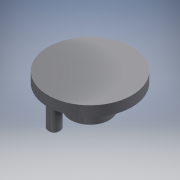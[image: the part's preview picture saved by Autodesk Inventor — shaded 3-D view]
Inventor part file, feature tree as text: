
AUTODESK INVENTOR PART (.ipt)
format: ipt  version: 2016 (Build 200138000, 138)  size: 146,944 bytes
history: native  units: mm
features: plane x4, extrude x4, sketch x3, reference x3, thicken_offset x2, chamfer x1, projected_geometry x1
ambient origin geometry x8: Origin, YZ Plane, XZ Plane, XY Plane, X Axis, Y Axis, Z Axis, Center Point
bodies: Solid1 (feature_tree)
feature tree (18):
  plane  "Work Plane1"
  extrude  "Extrusion1"  Depth=3.0mm TaperAngle=0.0deg
  extrude  "Extrusion2"  Depth=1.0mm TaperAngle=45.0deg
  chamfer  "Chamfer1"  Distance=2.0mm
  sketch  "Sketch3"  dims[d5=6.0mm d7=1.0mm d8=2.0mm d9=45.0deg d10=2.0mm d11=0.0mm]
  plane  "Work Plane2"
  plane  "Work Plane3"
  extrude  "Extrusion3"  Depth=10.0mm
  thicken_offset  "Thicken1"
  thicken_offset  "Thicken2"
  plane  "Work Plane4"
  extrude  "Extrusion5"  Depth=10.0mm
  sketch  "Sketch2"  dims[d1=10.0mm d2=0.0mm d3=3.0mm d4=0.0mm]
  projected_geometry  "Projected Loop2"
  reference  "Reference5"
  reference  "Reference6"
  reference  "Reference7"
  sketch  "Sketch5"  dims[d14=0.1mm d15=0.1mm d17=1.0mm d18=2.0mm d19=3.0mm d20=10.0mm d21=0.0mm d22=41.0mm]
